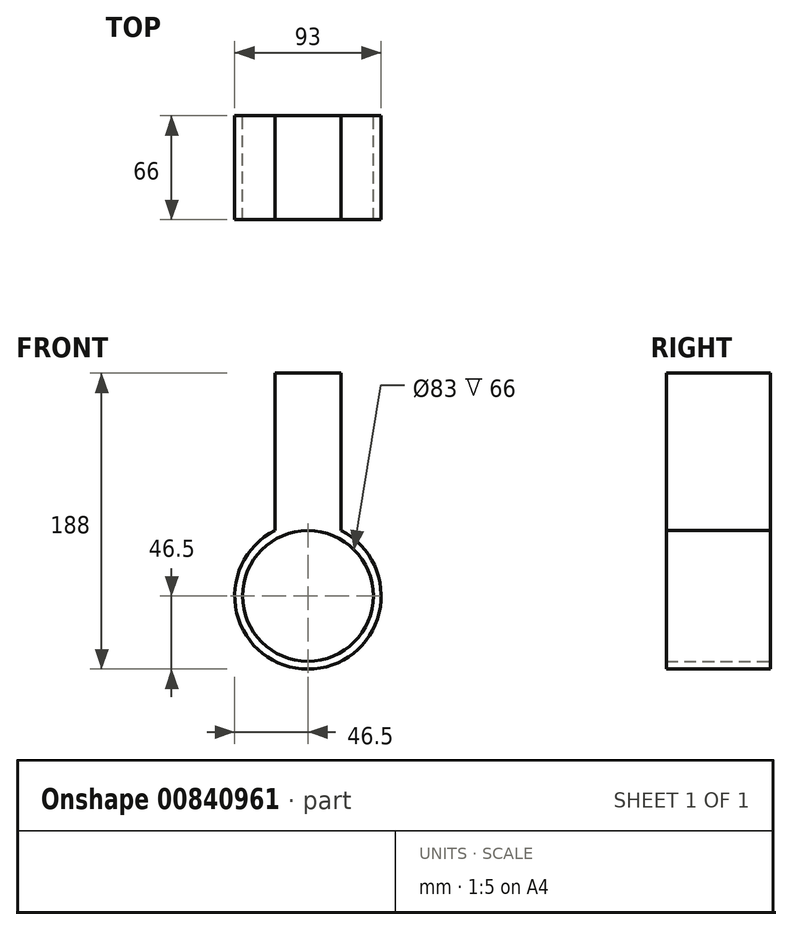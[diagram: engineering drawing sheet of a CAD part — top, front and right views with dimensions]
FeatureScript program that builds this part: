
annotation { "Feature Type Name" : "Feature", "Feature Type Description" : "" }
export const myFeature = defineFeature(function(context is Context, id is Id, definition is map)
    precondition{}
    {
        {
            var Q0;
            Q0=qCreatedBy(makeId("Front.planeOp"),FACE);
            var sketch = newSketch(context, id + "F0", { "sketchPlane" : qUnion([Q0])});
            skCircle(sketch, "E0", {"center": v(0, 0) * mm, "radius": 41.5 * mm});
            skCircle(sketch, "E1", {"center": v(0, 0) * mm, "radius": 46.5 * mm});
            skSolve(sketch);
        }
        {
            var Q0;
            Q0=makeQuery(id+"F0.imprint","IMPRINT",FACE,{"disambiguationData":[TD([[makeQuery(id+"F0.imprint","IMPRINT",EDGE,{"derivedFrom":sQuery(id+"F0.wireOp",EDGE,"E0")}),-1.0]])]});
            extrude(context, id + "F1", {"entities" : qUnion([Q0]), "depth" : 66 * mm, "offsetDistance" : 25 * mm});
        }
        {
            var Q0;
            Q0=makeQuery(id+"F1.opExtrude","CAP_FACE",FACE,{"disambiguationData":[OSD([sQuery(id+"F0.wireOp",EDGE,"E0"),sQuery(id+"F0.wireOp",EDGE,"E1")])],"isStart":false});
            cPlane(context, id + "F2", {"entities" : qUnion([Q0]), "cplaneType" : CPlaneType.OFFSET, "offset" : 0 * mm, "width" : 150 * mm, "height" : 150 * mm});
        }
        {
            var Q0;
            Q0=qCreatedBy(id+"F2.planeOp",FACE);
            var sketch = newSketch(context, id + "F3", { "sketchPlane" : qUnion([Q0])});
            skLineSegment(sketch, "E2.bottom", {"start": v(-21, 141.5) * mm, "end": v(21, 141.5) * mm});
            skLineSegment(sketch, "E2.top", {"start": v(-21, 41.5) * mm, "end": v(21, 41.5) * mm});
            skLineSegment(sketch, "E2.left", {"start": v(-21, 141.5) * mm, "end": v(-21, 41.5) * mm});
            skLineSegment(sketch, "E2.right", {"start": v(21, 141.5) * mm, "end": v(21, 41.5) * mm});
            skPoint(sketch, "E3", {"position": v(0, 41.5) * mm});
            skSolve(sketch);
        }
        {
            var Q0;
            Q0=makeQuery(id+"F3.imprint","IMPRINT",FACE,{"disambiguationData":[TD([[makeQuery(id+"F3.imprint","IMPRINT",EDGE,{"derivedFrom":sQuery(id+"F3.wireOp",EDGE,"E2.bottom")}),-1.0]])]});
            extrude(context, id + "F4", {"entities" : qUnion([Q0]), "operationType" : NewBodyOperationType.ADD, "oppositeDirection" : true, "depth" : 66 * mm, "offsetDistance" : 25 * mm});
        }
        {
            var Q0;
            Q0=qCreatedBy(makeId("Top.planeOp"),FACE);
            var sketch = newSketch(context, id + "F5", { "sketchPlane" : qUnion([Q0])});
            skLineSegment(sketch, "E4", {"start": v(-46.5, -66) * mm, "end": v(-46.5, 0) * mm});
            skLineSegment(sketch, "E5", {"start": v(46.5, 0) * mm, "end": v(46.5, -66) * mm});
            skLineSegment(sketch, "E6", {"start": v(-41.5, -66) * mm, "end": v(-41.5, 0) * mm});
            skLineSegment(sketch, "E7", {"start": v(41.5, 0) * mm, "end": v(41.5, -66) * mm});
            skSolve(sketch);
        }
        {
            var Q0;
            Q0=sQuery(id+"F5.wireOp",EDGE,"E5");
            cPlane(context, id + "F6", {"entities" : qUnion([Q0]), "cplaneType" : CPlaneType.LINE_ANGLE, "offset" : 25 * mm, "angle" : 90 * degree, "width" : 150 * mm, "height" : 150 * mm});
        }
    });
